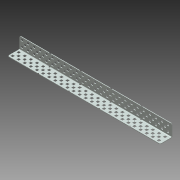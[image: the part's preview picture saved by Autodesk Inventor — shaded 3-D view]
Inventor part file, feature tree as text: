
AUTODESK INVENTOR PART (.ipt)
format: ipt  version: 2013 (Build 170138000, 138)  size: 1,414,656 bytes
history: native  units: mm (DEFAULTED — no unit token found)
features: other x154, extrude x148, sketch x10, sheet_metal_op x4, pattern_linear x4
ambient origin geometry x8: Origin, YZ Plane, XZ Plane, XY Plane, X Axis, Y Axis, Z Axis, Center Point
bodies: Solid1 (feature_tree)
feature tree (320):
  sheet_metal_op  "Face2"
  sheet_metal_op  "Flange8"
  pattern_linear  "Rectangular Pattern1"  Count1=24 Spacing1=12.7mm
  pattern_linear  "Rectangular Pattern2"  Spacing1=4.572mm  [1 undecoded]
  pattern_linear  "Rectangular Pattern3"  Spacing1=9.017mm  [1 undecoded]
  pattern_linear  "Rectangular Pattern4"  Spacing1=9.144mm  [1 undecoded]
  sketch  "Sketch1"  dims[d20=2.794mm]
  other  "Plate9"
  sketch  "Sketch14"  dims[d22=2.921mm]
  other  "Plate10"
  sheet_metal_op  "Bend8"
  sheet_metal_op  "Corner1"
  sketch  "Sketch15"  dims[d23=22.86mm]
  sketch  "Sketch16"  dims[d24=4.572mm]
  sketch  "Sketch17"  dims[d25=8.128mm]
  sketch  "Sketch18"  dims[d26=4.572mm]
  sketch  "Sketch19"  dims[d27=1.27mm]
  other  "Srf1"
  other  "Srf2"
  other  "Srf3"
  other  "Srf4"
  other  "Srf5"
  other  "Srf6"
  other  "Srf7"
  other  "Srf8"
  other  "Srf9"
  other  "Srf10"
  other  "Srf11"
  other  "Srf12"
  other  "Srf13"
  other  "Srf14"
  other  "Srf15"
  other  "Srf16"
  other  "Srf17"
  other  "Srf18"
  other  "Srf19"
  other  "Srf20"
  other  "Srf21"
  other  "Srf22"
  other  "Srf23"
  other  "Srf24"
  other  "Srf25"
  other  "Srf26"
  other  "Srf27"
  other  "Srf28"
  other  "Srf29"
  other  "Srf30"
  other  "Srf31"
  other  "Srf32"
  other  "Srf33"
  other  "Srf34"
  other  "Srf35"
  other  "Srf36"
  other  "Srf37"
  other  "Srf38"
  other  "Srf39"
  other  "Srf40"
  other  "Srf41"
  other  "Srf42"
  other  "Srf43"
  other  "Srf44"
  other  "Srf45"
  other  "Srf46"
  other  "Srf47"
  other  "Srf48"
  other  "Srf49"
  other  "Srf50"
  sketch  "Sketch20"  dims[d125=317.5mm]
  other  "Srf51"
  other  "Srf52"
  other  "Srf53"
  other  "Srf54"
  other  "Srf55"
  other  "Srf56"
  other  "Srf57"
  other  "Srf58"
  other  "Srf59"
  other  "Srf60"
  other  "Srf61"
  other  "Srf62"
  other  "Srf63"
  other  "Srf64"
  other  "Srf65"
  other  "Srf66"
  other  "Srf67"
  other  "Srf68"
  other  "Srf69"
  other  "Srf70"
  other  "Srf71"
  other  "Srf72"
  other  "Srf73"
  other  "Srf74"
  sketch  "Sketch21"  dims[d126=4.572mm]
  other  "Srf75"
  other  "Srf76"
  other  "Srf77"
  other  "Srf78"
  other  "Srf79"
  other  "Srf80"
  other  "Srf81"
  other  "Srf82"
  other  "Srf83"
  other  "Srf84"
  other  "Srf85"
  other  "Srf86"
  other  "Srf87"
  other  "Srf88"
  other  "Srf89"
  other  "Srf90"
  other  "Srf91"
  other  "Srf92"
  other  "Srf93"
  other  "Srf94"
  other  "Srf95"
  other  "Srf96"
  other  "Srf97"
  other  "Srf98"
  other  "Srf99"
  other  "Srf100"
  other  "Srf101"
  other  "Srf102"
  other  "Srf103"
  other  "Srf104"
  other  "Srf105"
  other  "Srf106"
  other  "Srf107"
  other  "Srf108"
  other  "Srf109"
  other  "Srf110"
  other  "Srf111"
  other  "Srf112"
  other  "Srf113"
  other  "Srf114"
  other  "Srf115"
  other  "Srf116"
  other  "Srf117"
  other  "Srf118"
  other  "Srf119"
  other  "Srf120"
  other  "Srf121"
  other  "Srf122"
  other  "Srf123"
  other  "Srf124"
  sketch  "Sketch22"  dims[d127=4.572mm d128=4.572mm d129=9.017mm d130=9.144mm d133=15.494mm d134=4.572mm d136=1.27mm d138=1.27mm d139=0.635mm d140=2.54mm d141=1.27mm d142=25.4mm d143=90.0deg d144=1.27mm d145=5.08mm d146=1.27mm d147=1.27mm d148=2.921mm d149=4.572mm d150=8.128mm d151=4.572mm d152=2.794mm d153=4.572mm d154=9.144mm d155=4.572mm d156=4.572mm d157=15.494mm d158=4.572mm d159=9.017mm d160=240.0mm d162=12.7mm d163=10.0mm d165=25.4mm d167=1.27mm d168=0.0mm d169=1.905mm d170=60.0mm d172=63.5mm d173=10.0mm d175=25.4mm d177=1.27mm d178=0.0mm d179=1.905mm d180=60.0mm d182=63.5mm d183=10.0mm d185=25.4mm d187=1.27mm d188=0.0mm d189=1.1176mm d190=1.905mm d191=40.0mm d193=63.5mm d194=10.0mm d196=25.4mm d198=1.27mm d199=0.0mm d200=25.4mm d201=0.0mm d202=250.0mm d204=12.7mm d205=20.0mm d207=12.7mm d208=25.4mm d209=0.0mm d210=240.0mm d212=12.7mm d213=0.0mm d214=0.0mm d215=0.0mm d216=0.0mm d217=0.0mm d218=0.0mm d219=0.0mm d220=0.0mm d221=0.0mm d222=0.0mm d223=0.0mm d224=0.0mm d225=0.0mm d226=0.0mm d227=0.0mm d228=0.0mm d229=0.0mm d230=0.0mm d231=0.0mm d232=0.0mm d233=0.0mm d234=0.0mm d235=0.0mm d236=0.0mm d237=0.0mm d238=0.0mm d239=0.0mm d240=0.0mm d241=0.0mm d242=0.0mm d243=0.0mm d244=0.0mm d245=0.0mm d246=0.0mm d247=0.0mm d248=0.0mm d249=0.0mm d250=0.0mm d251=0.0mm d252=0.0mm d253=0.0mm d254=0.0mm d255=0.0mm d256=0.0mm d257=0.0mm d258=0.0mm d259=0.0mm d260=0.0mm d261=0.0mm d262=0.0mm d263=0.0mm d264=0.0mm d265=0.0mm d266=0.0mm d267=0.0mm d268=0.0mm d269=0.0mm d270=0.0mm d271=0.0mm d272=0.0mm d273=0.0mm d274=0.0mm d275=0.0mm d276=0.0mm d277=0.0mm d278=0.0mm d279=0.0mm d280=0.0mm d281=0.0mm d282=0.0mm d283=0.0mm d284=0.0mm d285=0.0mm d286=0.0mm d287=0.0mm d288=0.0mm d289=0.0mm d290=0.0mm d291=0.0mm d292=0.0mm d293=0.0mm d294=0.0mm d295=0.0mm d296=0.0mm d297=0.0mm d298=0.0mm d299=0.0mm d300=0.0mm d301=0.0mm d302=0.0mm d303=0.0mm d304=0.0mm d305=0.0mm d306=0.0mm d307=0.0mm d308=0.0mm d309=0.0mm d310=0.0mm d311=0.0mm d312=0.0mm d313=0.0mm d314=0.0mm d315=0.0mm d316=0.0mm d317=0.0mm d318=0.0mm d319=0.0mm d320=0.0mm d321=0.0mm d322=0.0mm d323=0.0mm d324=0.0mm d325=0.0mm d326=0.0mm d327=0.0mm d328=0.0mm d329=0.0mm d330=0.0mm d331=0.0mm d332=0.0mm d333=0.0mm d334=0.0mm d335=0.0mm d336=0.0mm d337=0.0mm d338=0.0mm d339=0.0mm d340=0.0mm d341=0.0mm d342=0.0mm d343=0.0mm d344=0.0mm d345=0.0mm d346=0.0mm d347=0.0mm d348=0.0mm d349=0.0mm d350=0.0mm d351=0.0mm d352=0.0mm d353=0.0mm d354=0.0mm d355=0.0mm d356=0.0mm d357=0.0mm d358=0.0mm d359=0.0mm d360=25.4mm d361=0.0mm d362=250.0mm d364=12.7mm d365=20.0mm d367=12.7mm d368=25.4mm d369=0.0mm d370=240.0mm d372=12.7mm d373=0.0mm d374=0.0mm d375=0.0mm d376=0.0mm d377=0.0mm d378=0.0mm d379=0.0mm d380=0.0mm d381=0.0mm d382=0.0mm d383=0.0mm d384=0.0mm d385=0.0mm d386=0.0mm d387=0.0mm d388=0.0mm d389=0.0mm d390=0.0mm d391=0.0mm d392=0.0mm d393=0.0mm d394=0.0mm d395=0.0mm d396=0.0mm d397=0.0mm d398=0.0mm d399=0.0mm d400=0.0mm d401=0.0mm d402=0.0mm d403=0.0mm d404=0.0mm d405=0.0mm d406=0.0mm d407=0.0mm d408=0.0mm d409=0.0mm d410=0.0mm d411=0.0mm d412=0.0mm d413=0.0mm d414=0.0mm d415=0.0mm d416=0.0mm d417=0.0mm d418=0.0mm d419=0.0mm d420=0.0mm d421=0.0mm d422=0.0mm d423=0.0mm d424=0.0mm d425=0.0mm d426=0.0mm d427=0.0mm d428=0.0mm d429=0.0mm d430=0.0mm d431=0.0mm d432=0.0mm d433=0.0mm d434=0.0mm d435=0.0mm d436=0.0mm d437=0.0mm d438=0.0mm d439=0.0mm d440=0.0mm d441=0.0mm d442=0.0mm d443=0.0mm d444=0.0mm d445=0.0mm d446=0.0mm d447=0.0mm d448=0.0mm d449=0.0mm d450=0.0mm d451=0.0mm d452=0.0mm d453=0.0mm d454=0.0mm d455=0.0mm d456=0.0mm d457=0.0mm d458=0.0mm d459=0.0mm d460=0.0mm d461=0.0mm d462=0.0mm d463=0.0mm d464=0.0mm d465=0.0mm d466=0.0mm d467=0.0mm d468=0.0mm d469=0.0mm d470=0.0mm d471=0.0mm d472=0.0mm d473=0.0mm d474=0.0mm d475=0.0mm d476=0.0mm d477=0.0mm d478=0.0mm d479=0.0mm d480=0.0mm d481=0.0mm d482=0.0mm d483=0.0mm d484=0.0mm d485=0.0mm d486=0.0mm d487=0.0mm d488=0.0mm d489=0.0mm d490=0.0mm d491=0.0mm d492=0.0mm d493=0.0mm d494=0.0mm d495=0.0mm d496=0.0mm d497=0.0mm d498=0.0mm d499=0.0mm d500=0.0mm d501=0.0mm d502=0.0mm d503=0.0mm d504=0.0mm d505=0.0mm d506=0.0mm d507=0.0mm d508=0.0mm d509=0.0mm d510=0.0mm d511=0.0mm d512=0.0mm d513=0.0mm d514=0.0mm d515=0.0mm d516=0.0mm d517=0.0mm d518=0.0mm d519=0.0mm d520=0.0mm]
  other  "Srf125"
  other  "Srf126"
  other  "Srf127"
  other  "Srf128"
  other  "Srf129"
  other  "Srf130"
  other  "Srf131"
  other  "Srf132"
  other  "Srf133"
  other  "Srf134"
  other  "Srf135"
  other  "Srf136"
  other  "Srf137"
  other  "Srf138"
  other  "Srf139"
  other  "Srf140"
  other  "Srf141"
  other  "Srf142"
  other  "Srf143"
  other  "Srf144"
  other  "Srf145"
  other  "Srf146"
  other  "Srf147"
  other  "Srf148"
  other  "Cut4"
  other  "Cut5"
  other  "Cut6"
  other  "Cut7"
  extrude  "ExtrusionSrf1"  Depth=15.494mm
  extrude  "ExtrusionSrf51"  Depth=4.572mm
  extrude  "ExtrusionSrf75"  Depth=1.27mm
  extrude  "ExtrusionSrf125"  Depth=1.27mm
  extrude  "ExtrusionSrf2"  Depth=0.635mm
  extrude  "ExtrusionSrf3"  Depth=2.54mm
  extrude  "ExtrusionSrf4"  Depth=1.27mm
  extrude  "ExtrusionSrf5"  Depth=25.4mm TaperAngle=90.0deg
  extrude  "ExtrusionSrf6"  Depth=5.08mm
  extrude  "ExtrusionSrf7"  Depth=1.27mm
  extrude  "ExtrusionSrf8"  Depth=1.27mm
  extrude  "ExtrusionSrf9"  Depth=2.921mm
  extrude  "ExtrusionSrf10"  Depth=4.572mm
  extrude  "ExtrusionSrf11"  Depth=8.128mm
  extrude  "ExtrusionSrf12"  Depth=4.572mm
  extrude  "ExtrusionSrf13"  Depth=2.794mm
  extrude  "ExtrusionSrf14"  Depth=4.572mm
  extrude  "ExtrusionSrf15"  Depth=9.144mm
  extrude  "ExtrusionSrf16"  Depth=4.572mm
  extrude  "ExtrusionSrf17"  Depth=4.572mm
  extrude  "ExtrusionSrf18"  Depth=15.494mm
  extrude  "ExtrusionSrf19"  Depth=4.572mm
  extrude  "ExtrusionSrf20"  Depth=9.017mm
  extrude  "ExtrusionSrf21"  Depth=240.0mm
  extrude  "ExtrusionSrf22"  Depth=1.27mm
  extrude  "ExtrusionSrf23"  TaperAngle=0.0deg  [1 undecoded]
  extrude  "ExtrusionSrf24"  Depth=1.905mm
  extrude  "ExtrusionSrf25"  Depth=60.0mm
  extrude  "ExtrusionSrf26"  Depth=1.27mm
  extrude  "ExtrusionSrf27"  TaperAngle=0.0deg  [1 undecoded]
  extrude  "ExtrusionSrf28"  Depth=1.905mm
  extrude  "ExtrusionSrf29"  Depth=60.0mm
  extrude  "ExtrusionSrf30"  Depth=1.27mm
  extrude  "ExtrusionSrf31"  TaperAngle=0.0deg  [1 undecoded]
  extrude  "ExtrusionSrf32"  Depth=1.1176mm
  extrude  "ExtrusionSrf33"  Depth=1.905mm
  extrude  "ExtrusionSrf34"  Depth=40.0mm
  extrude  "ExtrusionSrf35"  Depth=1.27mm
  extrude  "ExtrusionSrf36"  TaperAngle=0.0deg  [1 undecoded]
  extrude  "ExtrusionSrf37"  Depth=25.4mm TaperAngle=0.0deg
  extrude  "ExtrusionSrf38"  Depth=250.0mm
  extrude  "ExtrusionSrf39"  Depth=20.0mm
  extrude  "ExtrusionSrf40"  Depth=25.4mm TaperAngle=0.0deg
  extrude  "ExtrusionSrf41"  Depth=240.0mm
  extrude  "ExtrusionSrf42"  TaperAngle=0.0deg  [1 undecoded]
  extrude  "ExtrusionSrf43"  TaperAngle=0.0deg  [1 undecoded]
  extrude  "ExtrusionSrf44"  TaperAngle=0.0deg  [1 undecoded]
  extrude  "ExtrusionSrf45"  TaperAngle=0.0deg  [1 undecoded]
  extrude  "ExtrusionSrf46"  TaperAngle=0.0deg  [1 undecoded]
  extrude  "ExtrusionSrf47"  TaperAngle=0.0deg  [1 undecoded]
  extrude  "ExtrusionSrf48"  TaperAngle=0.0deg  [1 undecoded]
  extrude  "ExtrusionSrf49"  TaperAngle=0.0deg  [1 undecoded]
  extrude  "ExtrusionSrf50"  TaperAngle=0.0deg  [1 undecoded]
  extrude  "ExtrusionSrf52"  TaperAngle=0.0deg  [1 undecoded]
  extrude  "ExtrusionSrf53"  TaperAngle=0.0deg  [1 undecoded]
  extrude  "ExtrusionSrf54"  TaperAngle=0.0deg  [1 undecoded]
  extrude  "ExtrusionSrf55"  TaperAngle=0.0deg  [1 undecoded]
  extrude  "ExtrusionSrf56"  TaperAngle=0.0deg  [1 undecoded]
  extrude  "ExtrusionSrf57"  TaperAngle=0.0deg  [1 undecoded]
  extrude  "ExtrusionSrf58"  TaperAngle=0.0deg  [1 undecoded]
  extrude  "ExtrusionSrf59"  TaperAngle=0.0deg  [1 undecoded]
  extrude  "ExtrusionSrf60"  TaperAngle=0.0deg  [1 undecoded]
  extrude  "ExtrusionSrf61"  TaperAngle=0.0deg  [1 undecoded]
  extrude  "ExtrusionSrf62"  TaperAngle=0.0deg  [1 undecoded]
  extrude  "ExtrusionSrf63"  TaperAngle=0.0deg  [1 undecoded]
  extrude  "ExtrusionSrf64"  TaperAngle=0.0deg  [1 undecoded]
  extrude  "ExtrusionSrf65"  TaperAngle=0.0deg  [1 undecoded]
  extrude  "ExtrusionSrf66"  TaperAngle=0.0deg  [1 undecoded]
  extrude  "ExtrusionSrf67"  TaperAngle=0.0deg  [1 undecoded]
  extrude  "ExtrusionSrf68"  TaperAngle=0.0deg  [1 undecoded]
  extrude  "ExtrusionSrf69"  TaperAngle=0.0deg  [1 undecoded]
  extrude  "ExtrusionSrf70"  TaperAngle=0.0deg  [1 undecoded]
  extrude  "ExtrusionSrf71"  TaperAngle=0.0deg  [1 undecoded]
  extrude  "ExtrusionSrf72"  TaperAngle=0.0deg  [1 undecoded]
  extrude  "ExtrusionSrf73"  TaperAngle=0.0deg  [1 undecoded]
  extrude  "ExtrusionSrf74"  TaperAngle=0.0deg  [1 undecoded]
  extrude  "ExtrusionSrf76"  TaperAngle=0.0deg  [1 undecoded]
  extrude  "ExtrusionSrf77"  TaperAngle=0.0deg  [1 undecoded]
  extrude  "ExtrusionSrf78"  TaperAngle=0.0deg  [1 undecoded]
  extrude  "ExtrusionSrf79"  TaperAngle=0.0deg  [1 undecoded]
  extrude  "ExtrusionSrf80"  TaperAngle=0.0deg  [1 undecoded]
  extrude  "ExtrusionSrf81"  TaperAngle=0.0deg  [1 undecoded]
  extrude  "ExtrusionSrf82"  TaperAngle=0.0deg  [1 undecoded]
  extrude  "ExtrusionSrf83"  TaperAngle=0.0deg  [1 undecoded]
  extrude  "ExtrusionSrf84"  TaperAngle=0.0deg  [1 undecoded]
  extrude  "ExtrusionSrf85"  TaperAngle=0.0deg  [1 undecoded]
  extrude  "ExtrusionSrf86"  TaperAngle=0.0deg  [1 undecoded]
  extrude  "ExtrusionSrf87"  TaperAngle=0.0deg  [1 undecoded]
  extrude  "ExtrusionSrf88"  TaperAngle=0.0deg  [1 undecoded]
  extrude  "ExtrusionSrf89"  TaperAngle=0.0deg  [1 undecoded]
  extrude  "ExtrusionSrf90"  TaperAngle=0.0deg  [1 undecoded]
  extrude  "ExtrusionSrf91"  TaperAngle=0.0deg  [1 undecoded]
  extrude  "ExtrusionSrf92"  TaperAngle=0.0deg  [1 undecoded]
  extrude  "ExtrusionSrf93"  TaperAngle=0.0deg  [1 undecoded]
  extrude  "ExtrusionSrf94"  TaperAngle=0.0deg  [1 undecoded]
  extrude  "ExtrusionSrf95"  TaperAngle=0.0deg  [1 undecoded]
  extrude  "ExtrusionSrf96"  TaperAngle=0.0deg  [1 undecoded]
  extrude  "ExtrusionSrf97"  TaperAngle=0.0deg  [1 undecoded]
  extrude  "ExtrusionSrf98"  TaperAngle=0.0deg  [1 undecoded]
  extrude  "ExtrusionSrf99"  TaperAngle=0.0deg  [1 undecoded]
  extrude  "ExtrusionSrf100"  TaperAngle=0.0deg  [1 undecoded]
  extrude  "ExtrusionSrf101"  TaperAngle=0.0deg  [1 undecoded]
  extrude  "ExtrusionSrf102"  TaperAngle=0.0deg  [1 undecoded]
  extrude  "ExtrusionSrf103"  TaperAngle=0.0deg  [1 undecoded]
  extrude  "ExtrusionSrf104"  TaperAngle=0.0deg  [1 undecoded]
  extrude  "ExtrusionSrf105"  TaperAngle=0.0deg  [1 undecoded]
  extrude  "ExtrusionSrf106"  TaperAngle=0.0deg  [1 undecoded]
  extrude  "ExtrusionSrf107"  TaperAngle=0.0deg  [1 undecoded]
  extrude  "ExtrusionSrf108"  TaperAngle=0.0deg  [1 undecoded]
  extrude  "ExtrusionSrf109"  TaperAngle=0.0deg  [1 undecoded]
  extrude  "ExtrusionSrf110"  TaperAngle=0.0deg  [1 undecoded]
  extrude  "ExtrusionSrf111"  TaperAngle=0.0deg  [1 undecoded]
  extrude  "ExtrusionSrf112"  TaperAngle=0.0deg  [1 undecoded]
  extrude  "ExtrusionSrf113"  TaperAngle=0.0deg  [1 undecoded]
  extrude  "ExtrusionSrf114"  TaperAngle=0.0deg  [1 undecoded]
  extrude  "ExtrusionSrf115"  TaperAngle=0.0deg  [1 undecoded]
  extrude  "ExtrusionSrf116"  TaperAngle=0.0deg  [1 undecoded]
  extrude  "ExtrusionSrf117"  TaperAngle=0.0deg  [1 undecoded]
  extrude  "ExtrusionSrf118"  TaperAngle=0.0deg  [1 undecoded]
  extrude  "ExtrusionSrf119"  TaperAngle=0.0deg  [1 undecoded]
  extrude  "ExtrusionSrf120"  TaperAngle=0.0deg  [1 undecoded]
  extrude  "ExtrusionSrf121"  TaperAngle=0.0deg  [1 undecoded]
  extrude  "ExtrusionSrf122"  TaperAngle=0.0deg  [1 undecoded]
  extrude  "ExtrusionSrf123"  TaperAngle=0.0deg  [1 undecoded]
  extrude  "ExtrusionSrf124"  TaperAngle=0.0deg  [1 undecoded]
  extrude  "ExtrusionSrf126"  TaperAngle=0.0deg  [1 undecoded]
  extrude  "ExtrusionSrf127"  TaperAngle=0.0deg  [1 undecoded]
  extrude  "ExtrusionSrf128"  TaperAngle=0.0deg  [1 undecoded]
  extrude  "ExtrusionSrf129"  TaperAngle=0.0deg  [1 undecoded]
  extrude  "ExtrusionSrf130"  TaperAngle=0.0deg  [1 undecoded]
  extrude  "ExtrusionSrf131"  TaperAngle=0.0deg  [1 undecoded]
  extrude  "ExtrusionSrf132"  TaperAngle=0.0deg  [1 undecoded]
  extrude  "ExtrusionSrf133"  TaperAngle=0.0deg  [1 undecoded]
  extrude  "ExtrusionSrf134"  TaperAngle=0.0deg  [1 undecoded]
  extrude  "ExtrusionSrf135"  TaperAngle=0.0deg  [1 undecoded]
  extrude  "ExtrusionSrf136"  TaperAngle=0.0deg  [1 undecoded]
  extrude  "ExtrusionSrf137"  TaperAngle=0.0deg  [1 undecoded]
  extrude  "ExtrusionSrf138"  TaperAngle=0.0deg  [1 undecoded]
  extrude  "ExtrusionSrf139"  TaperAngle=0.0deg  [1 undecoded]
  extrude  "ExtrusionSrf140"  TaperAngle=0.0deg  [1 undecoded]
  extrude  "ExtrusionSrf141"  TaperAngle=0.0deg  [1 undecoded]
  extrude  "ExtrusionSrf142"  TaperAngle=0.0deg  [1 undecoded]
  extrude  "ExtrusionSrf143"  TaperAngle=0.0deg  [1 undecoded]
  extrude  "ExtrusionSrf144"  TaperAngle=0.0deg  [1 undecoded]
  extrude  "ExtrusionSrf145"  TaperAngle=0.0deg  [1 undecoded]
  extrude  "ExtrusionSrf146"  TaperAngle=0.0deg  [1 undecoded]
  extrude  "ExtrusionSrf147"  TaperAngle=0.0deg  [1 undecoded]
  extrude  "ExtrusionSrf148"  TaperAngle=0.0deg  [1 undecoded]
note: 111 required parameter values undecoded (feature->parameter linkage not recoverable at this tier; creation-order binding heuristic only, values carry confidence <= 0.55)
